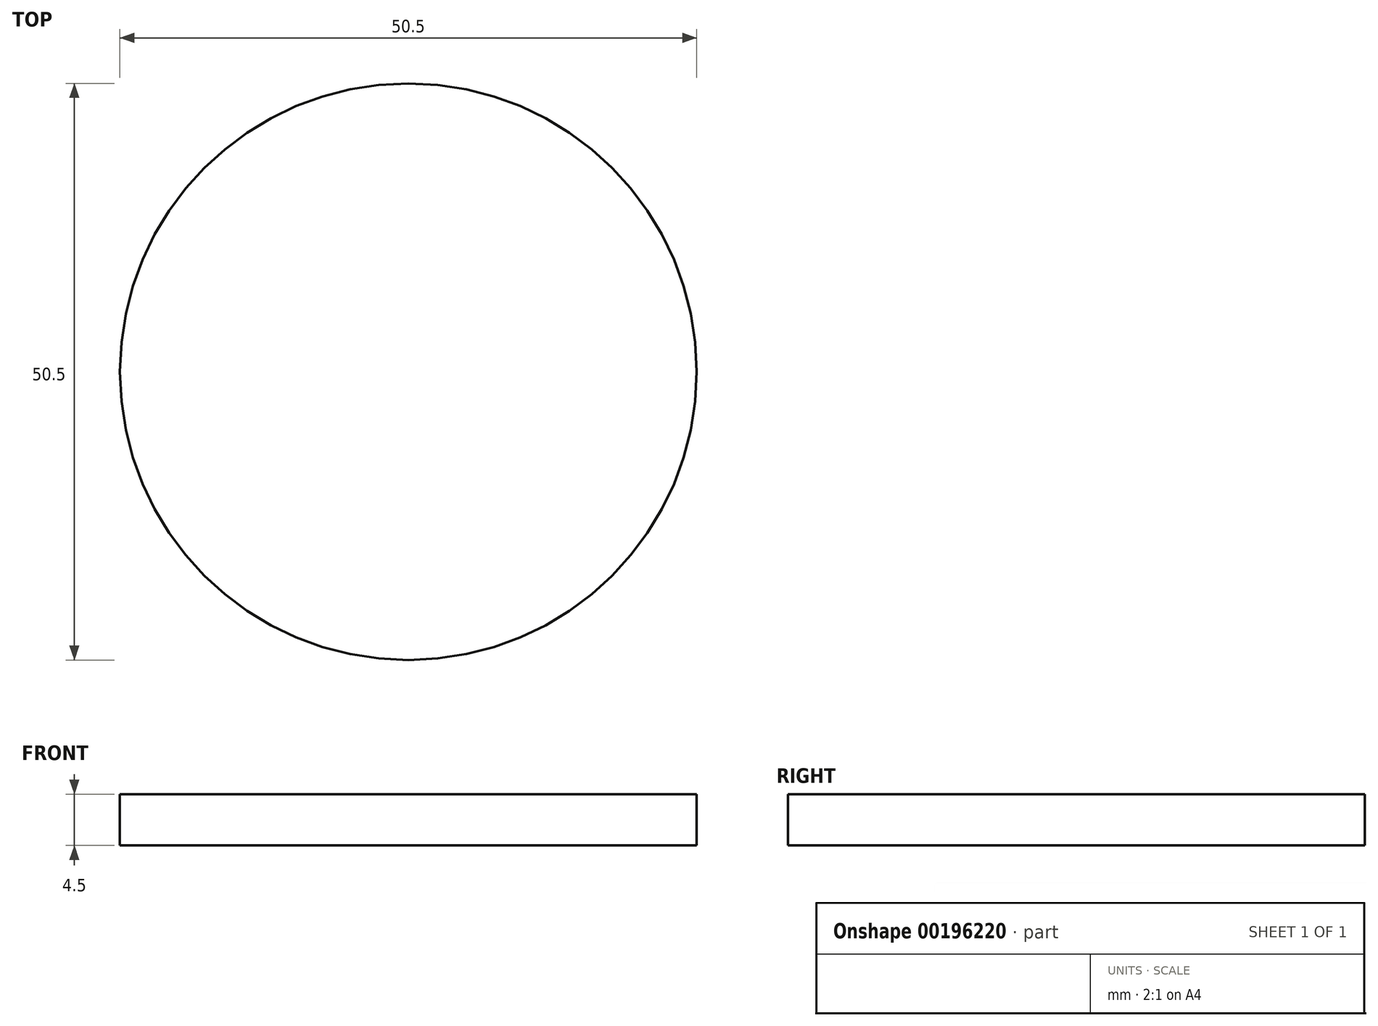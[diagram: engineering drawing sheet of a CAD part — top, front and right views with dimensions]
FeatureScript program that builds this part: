
annotation { "Feature Type Name" : "Feature", "Feature Type Description" : "" }
export const myFeature = defineFeature(function(context is Context, id is Id, definition is map)
    precondition{}
    {
        {
            var Q0;
            Q0=qCreatedBy(makeId("Top.planeOp"),FACE);
            var sketch = newSketch(context, id + "F0", { "sketchPlane" : qUnion([Q0])});
            skCircle(sketch, "E0", {"center": v(0, 0) * mm, "radius": 25.25 * mm});
            skSolve(sketch);
        }
        {
            var Q0;
            Q0=makeQuery(id+"F0.imprint","IMPRINT",FACE,{"disambiguationData":[TD([[makeQuery(id+"F0.imprint","IMPRINT",EDGE,{"derivedFrom":sQuery(id+"F0.wireOp",EDGE,"E0")}),1.0]])]});
            extrude(context, id + "F1", {"entities" : qUnion([Q0]), "depth" : 4.5 * mm});
        }
    });
